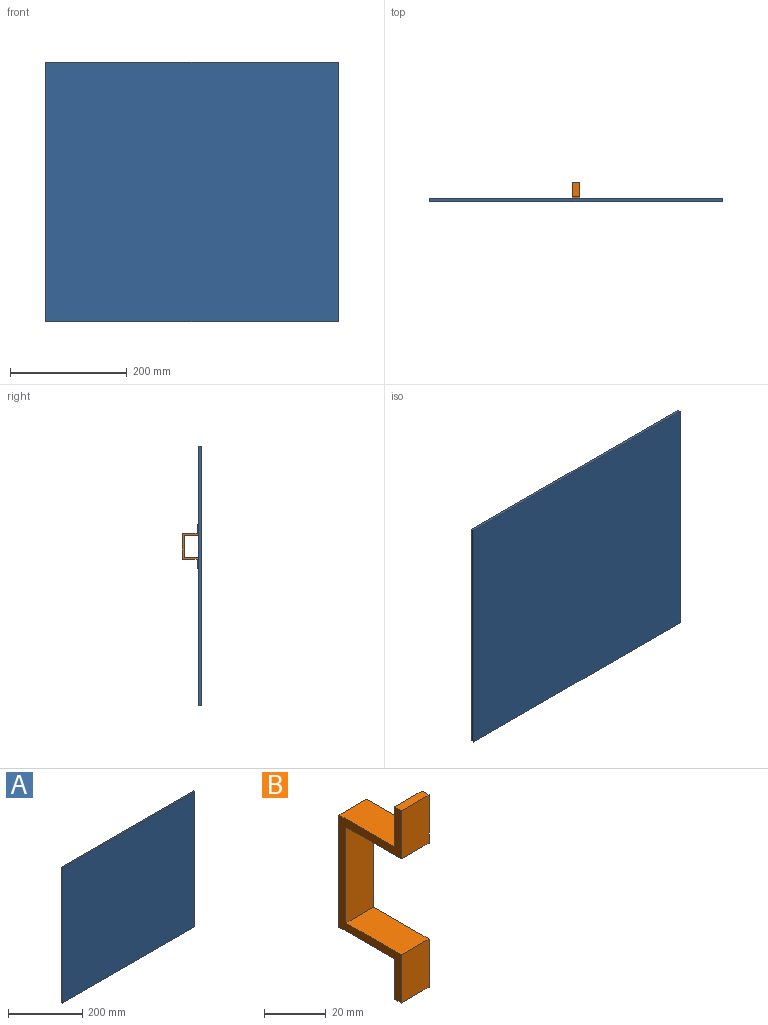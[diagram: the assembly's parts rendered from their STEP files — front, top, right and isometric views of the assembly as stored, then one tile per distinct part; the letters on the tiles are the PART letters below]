
ASSEMBLY  parts=2 mates=1
PART A: 6 faces, bbox 501.7x4.8x444.5 mm
  f0: plane 501.65x4.78mm, normal (0,0,-1), area 2395.5mm2, adj f1,f3,f4,f5
  f1: plane 501.65x444.5mm, normal (0,1,0), area 222983.4mm2, adj f0,f2,f4,f5
  f2: plane 501.65x4.78mm, normal (0,0,1), area 2395.5mm2, adj f1,f3,f4,f5
  f3: plane 501.65x444.5mm, normal (0,-1,0), area 222983.4mm2, adj f0,f2,f4,f5
  f4: plane 444.5x4.78mm, normal (1,0,0), area 2122.6mm2, adj f0,f1,f2,f3
  f5: plane 444.5x4.78mm, normal (-1,0,0), area 2122.6mm2, adj f0,f1,f2,f3
PART B: 14 faces, bbox 12.7x28.6x76.2 mm
  f0: plane 12.7x3.18mm, normal (0,0,1), area 40.3mm2, adj f1,f11,f12,f13
  f1: plane 19.05x12.7mm, normal (0,-1,0), area 241.9mm2, adj f0,f2,f12,f13
  f2: plane 25.4x12.7mm, normal (0,0,-1), area 322.6mm2, adj f1,f3,f12,f13
  f3: plane 38.1x12.7mm, normal (0,-1,0), area 483.9mm2, adj f2,f4,f12,f13
  f4: plane 25.4x12.7mm, normal (0,0,1), area 322.6mm2, adj f3,f5,f12,f13
  f5: plane 19.05x12.7mm, normal (0,-1,0), area 241.9mm2, adj f4,f6,f12,f13
  f6: plane 12.7x3.18mm, normal (0,0,-1), area 40.3mm2, adj f5,f7,f12,f13
  f7: plane 15.88x12.7mm, normal (0,1,0), area 201.6mm2, adj f6,f8,f12,f13
  f8: plane 25.4x12.7mm, normal (0,0,-1), area 322.6mm2, adj f7,f9,f12,f13
  f9: plane 44.45x12.7mm, normal (0,1,0), area 564.5mm2, adj f8,f10,f12,f13
  f10: plane 25.4x12.7mm, normal (0,0,1), area 322.6mm2, adj f9,f11,f12,f13
  f11: plane 15.88x12.7mm, normal (0,1,0), area 201.6mm2, adj f0,f10,f12,f13
  f12: plane 76.2x28.58mm, normal (1,0,0), area 403.2mm2, adj f0,f1,f2,f3,f4,f5,f6,f7
  f13: plane 76.2x28.58mm, normal (-1,0,0), area 403.2mm2, adj f0,f1,f2,f3,f4,f5,f6,f7
PLACE A rot(axis=(0,0,1),180deg) t=(152.44,450.94,-165.65)mm
PLACE B t=(-104.73,116.86,-139.14)mm
MATE fastened A.f3 <-> B.f5  axis (0,1,0) through (-98.38,116.86,262.87)mm
